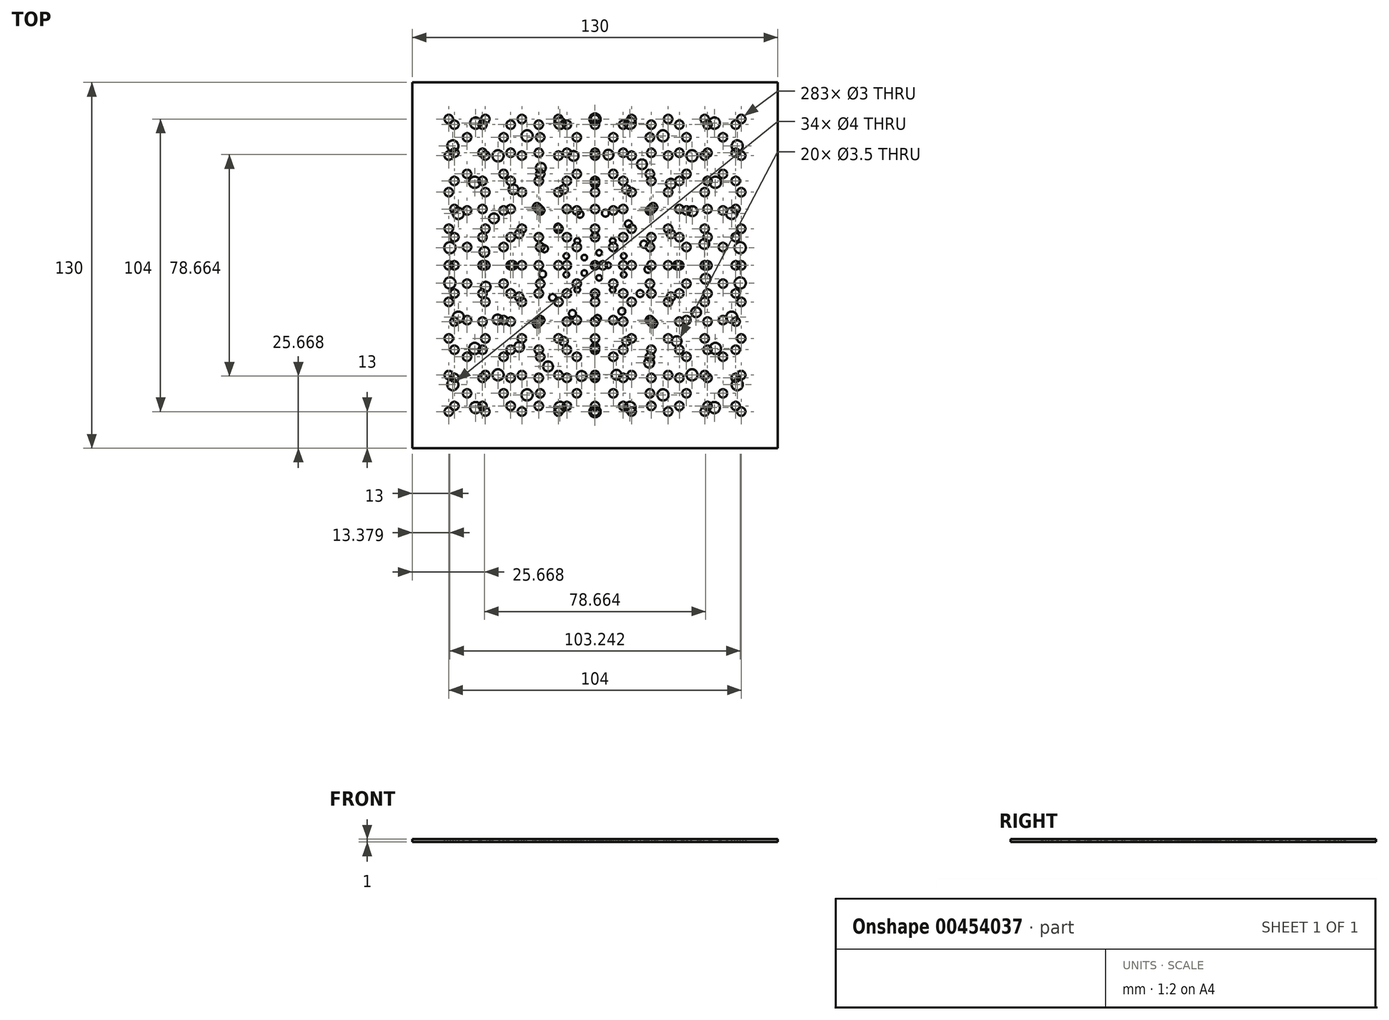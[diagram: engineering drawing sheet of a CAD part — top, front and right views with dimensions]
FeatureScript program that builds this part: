
annotation { "Feature Type Name" : "Feature", "Feature Type Description" : "" }
export const myFeature = defineFeature(function(context is Context, id is Id, definition is map)
    precondition{}
    {
        {
            var Q0;
            Q0=qCreatedBy(makeId("Top.planeOp"),FACE);
            var sketch = newSketch(context, id + "F0", { "sketchPlane" : qUnion([Q0])});
            skLineSegment(sketch, "E0.bottom", {"start": v(65, 65) * mm, "end": v(-65, 65) * mm});
            skLineSegment(sketch, "E0.top", {"start": v(65, -65) * mm, "end": v(-65, -65) * mm});
            skLineSegment(sketch, "E0.left", {"start": v(65, 65) * mm, "end": v(65, -65) * mm});
            skLineSegment(sketch, "E0.right", {"start": v(-65, 65) * mm, "end": v(-65, -65) * mm});
            skPoint(sketch, "E0.middle", {"position": v(0, 0) * mm});
            skLineSegment(sketch, "E1.bottom", {"start": v(55, 55) * mm, "end": v(-55, 55) * mm, "construction": true});
            skLineSegment(sketch, "E1.top", {"start": v(55, -55) * mm, "end": v(-55, -55) * mm, "construction": true});
            skLineSegment(sketch, "E1.left", {"start": v(55, 55) * mm, "end": v(55, -55) * mm, "construction": true});
            skLineSegment(sketch, "E1.right", {"start": v(-55, 55) * mm, "end": v(-55, -55) * mm, "construction": true});
            skCircle(sketch, "E2", {"center": v(0, 0) * mm, "radius": 1.5 * mm});
            skCircle(sketch, "E3.0.1.0", {"center": v(0, 10) * mm, "radius": 1.5 * mm});
            skCircle(sketch, "E3.0.2.0", {"center": v(0, 20) * mm, "radius": 1.5 * mm});
            skCircle(sketch, "E3.0.3.0", {"center": v(0, 30) * mm, "radius": 1.5 * mm});
            skCircle(sketch, "E3.0.4.0", {"center": v(0, 40) * mm, "radius": 1.5 * mm});
            skCircle(sketch, "E3.0.5.0", {"center": v(0, 50) * mm, "radius": 1.5 * mm});
            skCircle(sketch, "E3.1.0.0", {"center": v(10, 0) * mm, "radius": 1.5 * mm});
            skCircle(sketch, "E3.1.1.0", {"center": v(10, 10) * mm, "radius": 1.5 * mm});
            skCircle(sketch, "E3.1.2.0", {"center": v(10, 20) * mm, "radius": 1.5 * mm});
            skCircle(sketch, "E3.1.3.0", {"center": v(10, 30) * mm, "radius": 1.5 * mm});
            skCircle(sketch, "E3.1.4.0", {"center": v(10, 40) * mm, "radius": 1.5 * mm});
            skCircle(sketch, "E3.1.5.0", {"center": v(10, 50) * mm, "radius": 1.5 * mm});
            skCircle(sketch, "E3.2.0.0", {"center": v(20, 0) * mm, "radius": 1.5 * mm});
            skCircle(sketch, "E3.2.1.0", {"center": v(20, 10) * mm, "radius": 1.5 * mm});
            skCircle(sketch, "E3.2.2.0", {"center": v(20, 20) * mm, "radius": 1.5 * mm});
            skCircle(sketch, "E3.2.3.0", {"center": v(20, 30) * mm, "radius": 1.5 * mm});
            skCircle(sketch, "E3.2.4.0", {"center": v(20, 40) * mm, "radius": 1.5 * mm});
            skCircle(sketch, "E3.2.5.0", {"center": v(20, 50) * mm, "radius": 1.5 * mm});
            skCircle(sketch, "E3.3.0.0", {"center": v(30, 0) * mm, "radius": 1.5 * mm});
            skCircle(sketch, "E3.3.1.0", {"center": v(30, 10) * mm, "radius": 1.5 * mm});
            skCircle(sketch, "E3.3.2.0", {"center": v(30, 20) * mm, "radius": 1.5 * mm});
            skCircle(sketch, "E3.3.3.0", {"center": v(30, 30) * mm, "radius": 1.5 * mm});
            skCircle(sketch, "E3.3.4.0", {"center": v(30, 40) * mm, "radius": 1.5 * mm});
            skCircle(sketch, "E3.3.5.0", {"center": v(30, 50) * mm, "radius": 1.5 * mm});
            skCircle(sketch, "E3.4.0.0", {"center": v(40, 0) * mm, "radius": 1.5 * mm});
            skCircle(sketch, "E3.4.1.0", {"center": v(40, 10) * mm, "radius": 1.5 * mm});
            skCircle(sketch, "E3.4.2.0", {"center": v(40, 20) * mm, "radius": 1.5 * mm});
            skCircle(sketch, "E3.4.3.0", {"center": v(40, 30) * mm, "radius": 1.5 * mm});
            skCircle(sketch, "E3.4.4.0", {"center": v(40, 40) * mm, "radius": 1.5 * mm});
            skCircle(sketch, "E3.4.5.0", {"center": v(40, 50) * mm, "radius": 1.5 * mm});
            skCircle(sketch, "E3.5.0.0", {"center": v(50, 0) * mm, "radius": 1.5 * mm});
            skCircle(sketch, "E3.5.1.0", {"center": v(50, 10) * mm, "radius": 1.5 * mm});
            skCircle(sketch, "E3.5.2.0", {"center": v(50, 20) * mm, "radius": 1.5 * mm});
            skCircle(sketch, "E3.5.3.0", {"center": v(50, 30) * mm, "radius": 1.5 * mm});
            skCircle(sketch, "E3.5.4.0", {"center": v(50, 40) * mm, "radius": 1.5 * mm});
            skCircle(sketch, "E3.5.5.0", {"center": v(50, 50) * mm, "radius": 1.5 * mm});
            skLineSegment(sketch, "E3.direction1", {"start": v(0, 0) * mm, "end": v(10, 0) * mm, "construction": true});
            skLineSegment(sketch, "E3.direction2", {"start": v(0, 0) * mm, "end": v(0, 10) * mm, "construction": true});
            skCircle(sketch, "E4.0.1.0", {"center": v(0, -10) * mm, "radius": 1.5 * mm});
            skCircle(sketch, "E4.0.2.0", {"center": v(0, -20) * mm, "radius": 1.5 * mm});
            skCircle(sketch, "E4.0.3.0", {"center": v(0, -30) * mm, "radius": 1.5 * mm});
            skCircle(sketch, "E4.0.4.0", {"center": v(0, -40) * mm, "radius": 1.5 * mm});
            skCircle(sketch, "E4.0.5.0", {"center": v(0, -50) * mm, "radius": 1.5 * mm});
            skCircle(sketch, "E4.1.1.0", {"center": v(10, -10) * mm, "radius": 1.5 * mm});
            skCircle(sketch, "E4.1.2.0", {"center": v(10, -20) * mm, "radius": 1.5 * mm});
            skCircle(sketch, "E4.1.3.0", {"center": v(10, -30) * mm, "radius": 1.5 * mm});
            skCircle(sketch, "E4.1.4.0", {"center": v(10, -40) * mm, "radius": 1.5 * mm});
            skCircle(sketch, "E4.1.5.0", {"center": v(10, -50) * mm, "radius": 1.5 * mm});
            skCircle(sketch, "E4.2.1.0", {"center": v(20, -10) * mm, "radius": 1.5 * mm});
            skCircle(sketch, "E4.2.2.0", {"center": v(20, -20) * mm, "radius": 1.5 * mm});
            skCircle(sketch, "E4.2.3.0", {"center": v(20, -30) * mm, "radius": 1.5 * mm});
            skCircle(sketch, "E4.2.4.0", {"center": v(20, -40) * mm, "radius": 1.5 * mm});
            skCircle(sketch, "E4.2.5.0", {"center": v(20, -50) * mm, "radius": 1.5 * mm});
            skCircle(sketch, "E4.3.1.0", {"center": v(30, -10) * mm, "radius": 1.5 * mm});
            skCircle(sketch, "E4.3.2.0", {"center": v(30, -20) * mm, "radius": 1.5 * mm});
            skCircle(sketch, "E4.3.3.0", {"center": v(30, -30) * mm, "radius": 1.5 * mm});
            skCircle(sketch, "E4.3.4.0", {"center": v(30, -40) * mm, "radius": 1.5 * mm});
            skCircle(sketch, "E4.3.5.0", {"center": v(30, -50) * mm, "radius": 1.5 * mm});
            skCircle(sketch, "E4.4.1.0", {"center": v(40, -10) * mm, "radius": 1.5 * mm});
            skCircle(sketch, "E4.4.2.0", {"center": v(40, -20) * mm, "radius": 1.5 * mm});
            skCircle(sketch, "E4.4.3.0", {"center": v(40, -30) * mm, "radius": 1.5 * mm});
            skCircle(sketch, "E4.4.4.0", {"center": v(40, -40) * mm, "radius": 1.5 * mm});
            skCircle(sketch, "E4.4.5.0", {"center": v(40, -50) * mm, "radius": 1.5 * mm});
            skCircle(sketch, "E4.5.1.0", {"center": v(50, -10) * mm, "radius": 1.5 * mm});
            skCircle(sketch, "E4.5.2.0", {"center": v(50, -20) * mm, "radius": 1.5 * mm});
            skCircle(sketch, "E4.5.3.0", {"center": v(50, -30) * mm, "radius": 1.5 * mm});
            skCircle(sketch, "E4.5.4.0", {"center": v(50, -40) * mm, "radius": 1.5 * mm});
            skCircle(sketch, "E4.5.5.0", {"center": v(50, -50) * mm, "radius": 1.5 * mm});
            skLineSegment(sketch, "E4.direction2", {"start": v(0, 0) * mm, "end": v(0, -10) * mm, "construction": true});
            skCircle(sketch, "E5.1.0.0", {"center": v(-10, -50) * mm, "radius": 1.5 * mm});
            skCircle(sketch, "E5.1.1.0", {"center": v(-10, -40) * mm, "radius": 1.5 * mm});
            skCircle(sketch, "E5.1.2.0", {"center": v(-10, -30) * mm, "radius": 1.5 * mm});
            skCircle(sketch, "E5.1.3.0", {"center": v(-10, -20) * mm, "radius": 1.5 * mm});
            skCircle(sketch, "E5.1.4.0", {"center": v(-10, -10) * mm, "radius": 1.5 * mm});
            skCircle(sketch, "E5.1.5.0", {"center": v(-10, 0) * mm, "radius": 1.5 * mm});
            skCircle(sketch, "E5.1.6.0", {"center": v(-10, 10) * mm, "radius": 1.5 * mm});
            skCircle(sketch, "E5.1.7.0", {"center": v(-10, 20) * mm, "radius": 1.5 * mm});
            skCircle(sketch, "E5.1.8.0", {"center": v(-10, 30) * mm, "radius": 1.5 * mm});
            skCircle(sketch, "E5.1.9.0", {"center": v(-10, 40) * mm, "radius": 1.5 * mm});
            skCircle(sketch, "E5.1.10.0", {"center": v(-10, 50) * mm, "radius": 1.5 * mm});
            skCircle(sketch, "E5.2.0.0", {"center": v(-20, -50) * mm, "radius": 1.5 * mm});
            skCircle(sketch, "E5.2.1.0", {"center": v(-20, -40) * mm, "radius": 1.5 * mm});
            skCircle(sketch, "E5.2.2.0", {"center": v(-20, -30) * mm, "radius": 1.5 * mm});
            skCircle(sketch, "E5.2.3.0", {"center": v(-20, -20) * mm, "radius": 1.5 * mm});
            skCircle(sketch, "E5.2.4.0", {"center": v(-20, -10) * mm, "radius": 1.5 * mm});
            skCircle(sketch, "E5.2.5.0", {"center": v(-20, 0) * mm, "radius": 1.5 * mm});
            skCircle(sketch, "E5.2.6.0", {"center": v(-20, 10) * mm, "radius": 1.5 * mm});
            skCircle(sketch, "E5.2.7.0", {"center": v(-20, 20) * mm, "radius": 1.5 * mm});
            skCircle(sketch, "E5.2.8.0", {"center": v(-20, 30) * mm, "radius": 1.5 * mm});
            skCircle(sketch, "E5.2.9.0", {"center": v(-20, 40) * mm, "radius": 1.5 * mm});
            skCircle(sketch, "E5.2.10.0", {"center": v(-20, 50) * mm, "radius": 1.5 * mm});
            skCircle(sketch, "E5.3.0.0", {"center": v(-30, -50) * mm, "radius": 1.5 * mm});
            skCircle(sketch, "E5.3.1.0", {"center": v(-30, -40) * mm, "radius": 1.5 * mm});
            skCircle(sketch, "E5.3.2.0", {"center": v(-30, -30) * mm, "radius": 1.5 * mm});
            skCircle(sketch, "E5.3.3.0", {"center": v(-30, -20) * mm, "radius": 1.5 * mm});
            skCircle(sketch, "E5.3.4.0", {"center": v(-30, -10) * mm, "radius": 1.5 * mm});
            skCircle(sketch, "E5.3.5.0", {"center": v(-30, 0) * mm, "radius": 1.5 * mm});
            skCircle(sketch, "E5.3.6.0", {"center": v(-30, 10) * mm, "radius": 1.5 * mm});
            skCircle(sketch, "E5.3.7.0", {"center": v(-30, 20) * mm, "radius": 1.5 * mm});
            skCircle(sketch, "E5.3.8.0", {"center": v(-30, 30) * mm, "radius": 1.5 * mm});
            skCircle(sketch, "E5.3.9.0", {"center": v(-30, 40) * mm, "radius": 1.5 * mm});
            skCircle(sketch, "E5.3.10.0", {"center": v(-30, 50) * mm, "radius": 1.5 * mm});
            skCircle(sketch, "E5.4.0.0", {"center": v(-40, -50) * mm, "radius": 1.5 * mm});
            skCircle(sketch, "E5.4.1.0", {"center": v(-40, -40) * mm, "radius": 1.5 * mm});
            skCircle(sketch, "E5.4.2.0", {"center": v(-40, -30) * mm, "radius": 1.5 * mm});
            skCircle(sketch, "E5.4.3.0", {"center": v(-40, -20) * mm, "radius": 1.5 * mm});
            skCircle(sketch, "E5.4.4.0", {"center": v(-40, -10) * mm, "radius": 1.5 * mm});
            skCircle(sketch, "E5.4.5.0", {"center": v(-40, 0) * mm, "radius": 1.5 * mm});
            skCircle(sketch, "E5.4.6.0", {"center": v(-40, 10) * mm, "radius": 1.5 * mm});
            skCircle(sketch, "E5.4.7.0", {"center": v(-40, 20) * mm, "radius": 1.5 * mm});
            skCircle(sketch, "E5.4.8.0", {"center": v(-40, 30) * mm, "radius": 1.5 * mm});
            skCircle(sketch, "E5.4.9.0", {"center": v(-40, 40) * mm, "radius": 1.5 * mm});
            skCircle(sketch, "E5.4.10.0", {"center": v(-40, 50) * mm, "radius": 1.5 * mm});
            skCircle(sketch, "E5.5.0.0", {"center": v(-50, -50) * mm, "radius": 1.5 * mm});
            skCircle(sketch, "E5.5.1.0", {"center": v(-50, -40) * mm, "radius": 1.5 * mm});
            skCircle(sketch, "E5.5.2.0", {"center": v(-50, -30) * mm, "radius": 1.5 * mm});
            skCircle(sketch, "E5.5.3.0", {"center": v(-50, -20) * mm, "radius": 1.5 * mm});
            skCircle(sketch, "E5.5.4.0", {"center": v(-50, -10) * mm, "radius": 1.5 * mm});
            skCircle(sketch, "E5.5.5.0", {"center": v(-50, 0) * mm, "radius": 1.5 * mm});
            skCircle(sketch, "E5.5.6.0", {"center": v(-50, 10) * mm, "radius": 1.5 * mm});
            skCircle(sketch, "E5.5.7.0", {"center": v(-50, 20) * mm, "radius": 1.5 * mm});
            skCircle(sketch, "E5.5.8.0", {"center": v(-50, 30) * mm, "radius": 1.5 * mm});
            skCircle(sketch, "E5.5.9.0", {"center": v(-50, 40) * mm, "radius": 1.5 * mm});
            skCircle(sketch, "E5.5.10.0", {"center": v(-50, 50) * mm, "radius": 1.5 * mm});
            skLineSegment(sketch, "E5.direction1", {"start": v(0, -50) * mm, "end": v(-10, -50) * mm, "construction": true});
            skLineSegment(sketch, "E5.direction2", {"start": v(0, -50) * mm, "end": v(0, -40) * mm, "construction": true});
            skSolve(sketch);
        }
        {
            var Q0;
            Q0=makeQuery(id+"F0.imprint","IMPRINT",FACE,{"disambiguationData":[TD([[makeQuery(id+"F0.imprint","IMPRINT",EDGE,{"derivedFrom":sQuery(id+"F0.wireOp",EDGE,"E0.bottom")}),1.0]])]});
            extrude(context, id + "F1", {"entities" : qUnion([Q0]), "depth" : 1 * mm});
        }
        {
            var Q0;
            Q0=qCreatedBy(makeId("Top.planeOp"),FACE);
            var sketch = newSketch(context, id + "F2", { "sketchPlane" : qUnion([Q0])});
            skLineSegment(sketch, "E6.bottom", {"start": v(65, 65) * mm, "end": v(-65, 65) * mm});
            skLineSegment(sketch, "E6.top", {"start": v(65, -65) * mm, "end": v(-65, -65) * mm});
            skLineSegment(sketch, "E6.left", {"start": v(65, 65) * mm, "end": v(65, -65) * mm});
            skLineSegment(sketch, "E6.right", {"start": v(-65, 65) * mm, "end": v(-65, -65) * mm});
            skPoint(sketch, "E6.middle", {"position": v(0, 0) * mm});
            skLineSegment(sketch, "E7.bottom", {"start": v(55, 55) * mm, "end": v(-55, 55) * mm, "construction": true});
            skLineSegment(sketch, "E7.top", {"start": v(55, -55) * mm, "end": v(-55, -55) * mm, "construction": true});
            skLineSegment(sketch, "E7.left", {"start": v(55, 55) * mm, "end": v(55, -55) * mm, "construction": true});
            skLineSegment(sketch, "E7.right", {"start": v(-55, 55) * mm, "end": v(-55, -55) * mm, "construction": true});
            skCircle(sketch, "E8", {"center": v(0, 52) * mm, "radius": 2 * mm});
            skCircle(sketch, "E9.1.0", {"center": v(-12.44, 50.49) * mm, "radius": 2 * mm});
            skCircle(sketch, "E9.2.0", {"center": v(-24.17, 46.04) * mm, "radius": 2 * mm});
            skCircle(sketch, "E9.3.0", {"center": v(-34.48, 38.92) * mm, "radius": 2 * mm});
            skCircle(sketch, "E9.4.0", {"center": v(-42.8, 29.54) * mm, "radius": 2 * mm});
            skCircle(sketch, "E9.5.0", {"center": v(-48.62, 18.44) * mm, "radius": 2 * mm});
            skCircle(sketch, "E9.6.0", {"center": v(-51.62, 6.27) * mm, "radius": 2 * mm});
            skCircle(sketch, "E9.7.0", {"center": v(-51.62, -6.27) * mm, "radius": 2 * mm});
            skCircle(sketch, "E9.8.0", {"center": v(-48.62, -18.44) * mm, "radius": 2 * mm});
            skCircle(sketch, "E9.9.0", {"center": v(-42.8, -29.54) * mm, "radius": 2 * mm});
            skCircle(sketch, "E9.10.0", {"center": v(-34.48, -38.92) * mm, "radius": 2 * mm});
            skCircle(sketch, "E9.11.0", {"center": v(-24.17, -46.04) * mm, "radius": 2 * mm});
            skCircle(sketch, "E9.12.0", {"center": v(-12.44, -50.49) * mm, "radius": 2 * mm});
            skCircle(sketch, "E9.13.0", {"center": v(0, -52) * mm, "radius": 2 * mm});
            skCircle(sketch, "E9.14.0", {"center": v(12.44, -50.49) * mm, "radius": 2 * mm});
            skCircle(sketch, "E9.15.0", {"center": v(24.17, -46.04) * mm, "radius": 2 * mm});
            skCircle(sketch, "E9.16.0", {"center": v(34.48, -38.92) * mm, "radius": 2 * mm});
            skCircle(sketch, "E9.17.0", {"center": v(42.8, -29.54) * mm, "radius": 2 * mm});
            skCircle(sketch, "E9.18.0", {"center": v(48.62, -18.44) * mm, "radius": 2 * mm});
            skCircle(sketch, "E9.19.0", {"center": v(51.62, -6.27) * mm, "radius": 2 * mm});
            skLineSegment(sketch, "E10", {"start": v(0, 52) * mm, "end": v(12.44, 50.49) * mm, "construction": true});
            skLineSegment(sketch, "E11", {"start": v(0, 0) * mm, "end": v(6.22, 51.24) * mm, "construction": true});
            skCircle(sketch, "E12", {"center": v(4.78, 39.33) * mm, "radius": 1.75 * mm});
            skCircle(sketch, "E13.1.0", {"center": v(-7.61, 38.88) * mm, "radius": 1.75 * mm});
            skCircle(sketch, "E13.2.0", {"center": v(-19.26, 34.63) * mm, "radius": 1.75 * mm});
            skCircle(sketch, "E13.3.0", {"center": v(-29.01, 26.98) * mm, "radius": 1.75 * mm});
            skCircle(sketch, "E13.4.0", {"center": v(-35.93, 16.7) * mm, "radius": 1.75 * mm});
            skCircle(sketch, "E13.5.0", {"center": v(-39.33, 4.78) * mm, "radius": 1.75 * mm});
            skCircle(sketch, "E13.6.0", {"center": v(-38.88, -7.61) * mm, "radius": 1.75 * mm});
            skCircle(sketch, "E13.7.0", {"center": v(-34.63, -19.26) * mm, "radius": 1.75 * mm});
            skCircle(sketch, "E13.8.0", {"center": v(-26.98, -29.01) * mm, "radius": 1.75 * mm});
            skCircle(sketch, "E13.9.0", {"center": v(-16.7, -35.93) * mm, "radius": 1.75 * mm});
            skCircle(sketch, "E13.10.0", {"center": v(-4.78, -39.33) * mm, "radius": 1.75 * mm});
            skCircle(sketch, "E13.11.0", {"center": v(7.61, -38.88) * mm, "radius": 1.75 * mm});
            skCircle(sketch, "E13.12.0", {"center": v(19.26, -34.63) * mm, "radius": 1.75 * mm});
            skCircle(sketch, "E13.13.0", {"center": v(29.01, -26.98) * mm, "radius": 1.75 * mm});
            skCircle(sketch, "E13.14.0", {"center": v(35.93, -16.7) * mm, "radius": 1.75 * mm});
            skCircle(sketch, "E13.15.0", {"center": v(39.33, -4.78) * mm, "radius": 1.75 * mm});
            skCircle(sketch, "E13.16.0", {"center": v(38.88, 7.61) * mm, "radius": 1.75 * mm});
            skCircle(sketch, "E13.17.0", {"center": v(34.63, 19.26) * mm, "radius": 1.75 * mm});
            skCircle(sketch, "E13.18.0", {"center": v(26.98, 29.01) * mm, "radius": 1.75 * mm});
            skCircle(sketch, "E13.19.0", {"center": v(16.7, 35.93) * mm, "radius": 1.75 * mm});
            skCircle(sketch, "E14", {"center": v(0, 29.2) * mm, "radius": 1.5 * mm});
            skCircle(sketch, "E15.1.0", {"center": v(-11.17, 26.98) * mm, "radius": 1.5 * mm});
            skCircle(sketch, "E15.2.0", {"center": v(-20.65, 20.65) * mm, "radius": 1.5 * mm});
            skCircle(sketch, "E15.3.0", {"center": v(-26.98, 11.17) * mm, "radius": 1.5 * mm});
            skCircle(sketch, "E15.4.0", {"center": v(-29.2, 0) * mm, "radius": 1.5 * mm});
            skCircle(sketch, "E15.5.0", {"center": v(-26.98, -11.17) * mm, "radius": 1.5 * mm});
            skCircle(sketch, "E15.6.0", {"center": v(-20.65, -20.65) * mm, "radius": 1.5 * mm});
            skCircle(sketch, "E15.7.0", {"center": v(-11.17, -26.98) * mm, "radius": 1.5 * mm});
            skCircle(sketch, "E15.8.0", {"center": v(0, -29.2) * mm, "radius": 1.5 * mm});
            skCircle(sketch, "E15.9.0", {"center": v(11.17, -26.98) * mm, "radius": 1.5 * mm});
            skCircle(sketch, "E15.10.0", {"center": v(20.65, -20.65) * mm, "radius": 1.5 * mm});
            skCircle(sketch, "E15.11.0", {"center": v(26.98, -11.17) * mm, "radius": 1.5 * mm});
            skCircle(sketch, "E15.12.0", {"center": v(29.2, 0) * mm, "radius": 1.5 * mm});
            skCircle(sketch, "E15.13.0", {"center": v(26.98, 11.17) * mm, "radius": 1.5 * mm});
            skCircle(sketch, "E15.14.0", {"center": v(20.65, 20.65) * mm, "radius": 1.5 * mm});
            skCircle(sketch, "E16.1.20.0", {"center": v(51.62, 6.27) * mm, "radius": 2 * mm});
            skCircle(sketch, "E16.1.21.0", {"center": v(48.62, 18.44) * mm, "radius": 2 * mm});
            skCircle(sketch, "E16.1.22.0", {"center": v(42.8, 29.54) * mm, "radius": 2 * mm});
            skCircle(sketch, "E16.1.23.0", {"center": v(34.48, 38.92) * mm, "radius": 2 * mm});
            skCircle(sketch, "E16.1.24.0", {"center": v(24.17, 46.04) * mm, "radius": 2 * mm});
            skLineSegment(sketch, "E17", {"start": v(0, 29.2) * mm, "end": v(11.17, 26.98) * mm, "construction": true});
            skLineSegment(sketch, "E18", {"start": v(0, 0) * mm, "end": v(5.59, 28.09) * mm, "construction": true});
            skCircle(sketch, "E19", {"center": v(3.7, 18.56) * mm, "radius": 1.25 * mm});
            skCircle(sketch, "E20.1.0", {"center": v(-5.35, 18.15) * mm, "radius": 1.25 * mm});
            skCircle(sketch, "E20.2.0", {"center": v(-13.17, 13.58) * mm, "radius": 1.25 * mm});
            skCircle(sketch, "E20.3.0", {"center": v(-17.98, 5.9) * mm, "radius": 1.25 * mm});
            skCircle(sketch, "E20.4.0", {"center": v(-18.66, -3.13) * mm, "radius": 1.25 * mm});
            skCircle(sketch, "E20.5.0", {"center": v(-15.07, -11.44) * mm, "radius": 1.25 * mm});
            skCircle(sketch, "E20.6.0", {"center": v(-8.02, -17.13) * mm, "radius": 1.25 * mm});
            skCircle(sketch, "E20.7.0", {"center": v(0.86, -18.9) * mm, "radius": 1.25 * mm});
            skCircle(sketch, "E20.8.0", {"center": v(9.54, -16.34) * mm, "radius": 1.25 * mm});
            skCircle(sketch, "E20.9.0", {"center": v(16.04, -10.03) * mm, "radius": 1.25 * mm});
            skCircle(sketch, "E21", {"center": v(0, 10.73) * mm, "radius": 1 * mm});
            skCircle(sketch, "E22.1.0", {"center": v(-6.3, 8.68) * mm, "radius": 1 * mm});
            skCircle(sketch, "E22.2.0", {"center": v(-10.2, 3.32) * mm, "radius": 1 * mm});
            skCircle(sketch, "E22.3.0", {"center": v(-10.2, -3.32) * mm, "radius": 1 * mm});
            skCircle(sketch, "E22.4.0", {"center": v(-6.3, -8.68) * mm, "radius": 1 * mm});
            skCircle(sketch, "E23.1.15.0", {"center": v(11.17, 26.98) * mm, "radius": 1.5 * mm});
            skCircle(sketch, "E24.1.10.0", {"center": v(18.87, -1.43) * mm, "radius": 1.25 * mm});
            skCircle(sketch, "E24.1.11.0", {"center": v(17.37, 7.5) * mm, "radius": 1.25 * mm});
            skCircle(sketch, "E25.1.5.0", {"center": v(0, -10.73) * mm, "radius": 1 * mm});
            skCircle(sketch, "E25.1.6.0", {"center": v(6.3, -8.68) * mm, "radius": 1 * mm});
            skCircle(sketch, "E25.1.7.0", {"center": v(10.2, -3.32) * mm, "radius": 1 * mm});
            skCircle(sketch, "E25.1.8.0", {"center": v(10.2, 3.32) * mm, "radius": 1 * mm});
            skCircle(sketch, "E25.1.9.0", {"center": v(6.3, 8.68) * mm, "radius": 1 * mm});
            skCircle(sketch, "E26.1.12.0", {"center": v(11.9, 14.71) * mm, "radius": 1.25 * mm});
            skCircle(sketch, "E27.1.25.0", {"center": v(12.44, 50.49) * mm, "radius": 2 * mm});
            skLineSegment(sketch, "E28", {"start": v(0, 10.73) * mm, "end": v(6.3, 8.68) * mm, "construction": true});
            skLineSegment(sketch, "E29", {"start": v(0, 0) * mm, "end": v(3.15, 9.7) * mm, "construction": true});
            skCircle(sketch, "E30", {"center": v(1.45, 4.47) * mm, "radius": 1 * mm});
            skCircle(sketch, "E31.1.0", {"center": v(-3.8, 2.77) * mm, "radius": 1 * mm});
            skCircle(sketch, "E31.2.0", {"center": v(-3.8, -2.77) * mm, "radius": 1 * mm});
            skCircle(sketch, "E31.3.0", {"center": v(1.45, -4.47) * mm, "radius": 1 * mm});
            skCircle(sketch, "E31.4.0", {"center": v(4.7, 0) * mm, "radius": 1 * mm});
            skCircle(sketch, "E32", {"center": v(0, 0) * mm, "radius": 1 * mm});
            skPoint(sketch, "E33.centerSnap0", {"position": v(0, 65) * mm});
            skCircle(sketch, "E34.4.0", {"center": v(-42.42, 50.56) * mm, "radius": 2 * mm});
            skCircle(sketch, "E34.5.0", {"center": v(-50.56, 42.42) * mm, "radius": 2 * mm});
            skCircle(sketch, "E34.13.0", {"center": v(-50.56, -42.42) * mm, "radius": 2 * mm});
            skCircle(sketch, "E34.14.0", {"center": v(-42.42, -50.56) * mm, "radius": 2 * mm});
            skCircle(sketch, "E34.22.0", {"center": v(42.42, -50.56) * mm, "radius": 2 * mm});
            skCircle(sketch, "E34.23.0", {"center": v(50.56, -42.42) * mm, "radius": 2 * mm});
            skCircle(sketch, "E34.31.0", {"center": v(50.56, 42.42) * mm, "radius": 2 * mm});
            skCircle(sketch, "E35.1.32.0", {"center": v(42.42, 50.56) * mm, "radius": 2 * mm});
            skSolve(sketch);
        }
        {
            var Q0;
            Q0=makeQuery(id+"F2.imprint","IMPRINT",FACE,{"disambiguationData":[TD([[makeQuery(id+"F2.imprint","IMPRINT",EDGE,{"derivedFrom":sQuery(id+"F2.wireOp",EDGE,"E6.bottom")}),1.0]])]});
            extrude(context, id + "F3", {"entities" : qUnion([Q0]), "depth" : 1 * mm});
        }
        {
            var Q0;
            Q0=qCreatedBy(makeId("Top.planeOp"),FACE);
            var sketch = newSketch(context, id + "F4", { "sketchPlane" : qUnion([Q0])});
            skLineSegment(sketch, "E36.bottom", {"start": v(65, -65) * mm, "end": v(-65, -65) * mm});
            skLineSegment(sketch, "E36.top", {"start": v(65, 65) * mm, "end": v(-65, 65) * mm});
            skLineSegment(sketch, "E36.left", {"start": v(65, -65) * mm, "end": v(65, 65) * mm});
            skLineSegment(sketch, "E36.right", {"start": v(-65, -65) * mm, "end": v(-65, 65) * mm});
            skPoint(sketch, "E36.middle", {"position": v(0, 0) * mm});
            skLineSegment(sketch, "E37.bottom", {"start": v(55, -55) * mm, "end": v(-55, -55) * mm, "construction": true});
            skLineSegment(sketch, "E37.top", {"start": v(55, 55) * mm, "end": v(-55, 55) * mm, "construction": true});
            skLineSegment(sketch, "E37.left", {"start": v(55, -55) * mm, "end": v(55, 55) * mm, "construction": true});
            skLineSegment(sketch, "E37.right", {"start": v(-55, -55) * mm, "end": v(-55, 55) * mm, "construction": true});
            skCircle(sketch, "E38", {"center": v(0, 0) * mm, "radius": 1.5 * mm});
            skCircle(sketch, "E39", {"center": v(13, 0) * mm, "radius": 1.5 * mm});
            skLineSegment(sketch, "E40", {"start": v(0, 0) * mm, "end": v(13, 0) * mm, "construction": true});
            skLineSegment(sketch, "E41", {"start": v(6.5, 0) * mm, "end": v(6.5, 6.5) * mm, "construction": true});
            skLineSegment(sketch, "E42", {"start": v(6.5, 6.5) * mm, "end": v(0, 0) * mm, "construction": true});
            skCircle(sketch, "E43", {"center": v(6.5, 6.5) * mm, "radius": 1.5 * mm});
            skCircle(sketch, "E44.0.1.0", {"center": v(0, 13) * mm, "radius": 1.5 * mm});
            skCircle(sketch, "E44.0.1.1", {"center": v(6.5, 19.5) * mm, "radius": 1.5 * mm});
            skCircle(sketch, "E44.0.2.0", {"center": v(0, 26) * mm, "radius": 1.5 * mm});
            skCircle(sketch, "E44.0.2.1", {"center": v(6.5, 32.5) * mm, "radius": 1.5 * mm});
            skCircle(sketch, "E44.0.3.0", {"center": v(0, 39) * mm, "radius": 1.5 * mm});
            skCircle(sketch, "E44.0.3.1", {"center": v(6.5, 45.5) * mm, "radius": 1.5 * mm});
            skCircle(sketch, "E44.0.4.0", {"center": v(0, 52) * mm, "radius": 1.5 * mm});
            skCircle(sketch, "E44.1.0.1", {"center": v(19.5, 6.5) * mm, "radius": 1.5 * mm});
            skCircle(sketch, "E44.1.1.0", {"center": v(13, 13) * mm, "radius": 1.5 * mm});
            skCircle(sketch, "E44.1.1.1", {"center": v(19.5, 19.5) * mm, "radius": 1.5 * mm});
            skCircle(sketch, "E44.1.2.0", {"center": v(13, 26) * mm, "radius": 1.5 * mm});
            skCircle(sketch, "E44.1.2.1", {"center": v(19.5, 32.5) * mm, "radius": 1.5 * mm});
            skCircle(sketch, "E44.1.3.0", {"center": v(13, 39) * mm, "radius": 1.5 * mm});
            skCircle(sketch, "E44.1.3.1", {"center": v(19.5, 45.5) * mm, "radius": 1.5 * mm});
            skCircle(sketch, "E44.1.4.0", {"center": v(13, 52) * mm, "radius": 1.5 * mm});
            skCircle(sketch, "E44.2.0.0", {"center": v(26, 0) * mm, "radius": 1.5 * mm});
            skCircle(sketch, "E44.2.0.1", {"center": v(32.5, 6.5) * mm, "radius": 1.5 * mm});
            skCircle(sketch, "E44.2.1.0", {"center": v(26, 13) * mm, "radius": 1.5 * mm});
            skCircle(sketch, "E44.2.1.1", {"center": v(32.5, 19.5) * mm, "radius": 1.5 * mm});
            skCircle(sketch, "E44.2.2.0", {"center": v(26, 26) * mm, "radius": 1.5 * mm});
            skCircle(sketch, "E44.2.2.1", {"center": v(32.5, 32.5) * mm, "radius": 1.5 * mm});
            skCircle(sketch, "E44.2.3.0", {"center": v(26, 39) * mm, "radius": 1.5 * mm});
            skCircle(sketch, "E44.2.3.1", {"center": v(32.5, 45.5) * mm, "radius": 1.5 * mm});
            skCircle(sketch, "E44.2.4.0", {"center": v(26, 52) * mm, "radius": 1.5 * mm});
            skCircle(sketch, "E44.3.0.0", {"center": v(39, 0) * mm, "radius": 1.5 * mm});
            skCircle(sketch, "E44.3.0.1", {"center": v(45.5, 6.5) * mm, "radius": 1.5 * mm});
            skCircle(sketch, "E44.3.1.0", {"center": v(39, 13) * mm, "radius": 1.5 * mm});
            skCircle(sketch, "E44.3.1.1", {"center": v(45.5, 19.5) * mm, "radius": 1.5 * mm});
            skCircle(sketch, "E44.3.2.0", {"center": v(39, 26) * mm, "radius": 1.5 * mm});
            skCircle(sketch, "E44.3.2.1", {"center": v(45.5, 32.5) * mm, "radius": 1.5 * mm});
            skCircle(sketch, "E44.3.3.0", {"center": v(39, 39) * mm, "radius": 1.5 * mm});
            skCircle(sketch, "E44.3.3.1", {"center": v(45.5, 45.5) * mm, "radius": 1.5 * mm});
            skCircle(sketch, "E44.3.4.0", {"center": v(39, 52) * mm, "radius": 1.5 * mm});
            skCircle(sketch, "E44.4.0.0", {"center": v(52, 0) * mm, "radius": 1.5 * mm});
            skCircle(sketch, "E44.4.1.0", {"center": v(52, 13) * mm, "radius": 1.5 * mm});
            skCircle(sketch, "E44.4.2.0", {"center": v(52, 26) * mm, "radius": 1.5 * mm});
            skCircle(sketch, "E44.4.3.0", {"center": v(52, 39) * mm, "radius": 1.5 * mm});
            skCircle(sketch, "E44.4.4.0", {"center": v(52, 52) * mm, "radius": 1.5 * mm});
            skLineSegment(sketch, "E44.direction2", {"start": v(0, 0) * mm, "end": v(0, 13) * mm, "construction": true});
            skCircle(sketch, "E45.MirrorC", {"center": v(-13, 0) * mm, "radius": 1.5 * mm});
            skCircle(sketch, "E46.MirrorC", {"center": v(-6.5, 6.5) * mm, "radius": 1.5 * mm});
            skCircle(sketch, "E47.MirrorC", {"center": v(-45.5, 32.5) * mm, "radius": 1.5 * mm});
            skCircle(sketch, "E48.MirrorC", {"center": v(-6.5, 19.5) * mm, "radius": 1.5 * mm});
            skCircle(sketch, "E49.MirrorC", {"center": v(-52, 13) * mm, "radius": 1.5 * mm});
            skCircle(sketch, "E50.MirrorC", {"center": v(-26, 39) * mm, "radius": 1.5 * mm});
            skCircle(sketch, "E51.MirrorC", {"center": v(-19.5, 32.5) * mm, "radius": 1.5 * mm});
            skCircle(sketch, "E52.MirrorC", {"center": v(-45.5, 6.5) * mm, "radius": 1.5 * mm});
            skCircle(sketch, "E53.MirrorC", {"center": v(-39, 39) * mm, "radius": 1.5 * mm});
            skCircle(sketch, "E54.MirrorC", {"center": v(-26, 0) * mm, "radius": 1.5 * mm});
            skCircle(sketch, "E55.MirrorC", {"center": v(-19.5, 6.5) * mm, "radius": 1.5 * mm});
            skCircle(sketch, "E56.MirrorC", {"center": v(-45.5, 19.5) * mm, "radius": 1.5 * mm});
            skCircle(sketch, "E57.MirrorC", {"center": v(-52, 0) * mm, "radius": 1.5 * mm});
            skCircle(sketch, "E58.MirrorC", {"center": v(-26, 26) * mm, "radius": 1.5 * mm});
            skCircle(sketch, "E59.MirrorC", {"center": v(-19.5, 45.5) * mm, "radius": 1.5 * mm});
            skLineSegment(sketch, "E60.MirrorCS", {"start": v(-6.5, 0) * mm, "end": v(-6.5, 6.5) * mm, "construction": true});
            skCircle(sketch, "E61.MirrorC", {"center": v(-26, 52) * mm, "radius": 1.5 * mm});
            skCircle(sketch, "E62.MirrorC", {"center": v(-52, 26) * mm, "radius": 1.5 * mm});
            skCircle(sketch, "E63.MirrorC", {"center": v(-13, 13) * mm, "radius": 1.5 * mm});
            skCircle(sketch, "E64.MirrorC", {"center": v(-32.5, 45.5) * mm, "radius": 1.5 * mm});
            skCircle(sketch, "E65.MirrorC", {"center": v(-6.5, 45.5) * mm, "radius": 1.5 * mm});
            skCircle(sketch, "E66.MirrorC", {"center": v(-32.5, 19.5) * mm, "radius": 1.5 * mm});
            skCircle(sketch, "E67.MirrorC", {"center": v(-39, 0) * mm, "radius": 1.5 * mm});
            skCircle(sketch, "E68.MirrorC", {"center": v(-13, 26) * mm, "radius": 1.5 * mm});
            skCircle(sketch, "E69.MirrorC", {"center": v(-52, 39) * mm, "radius": 1.5 * mm});
            skCircle(sketch, "E70.MirrorC", {"center": v(-26, 13) * mm, "radius": 1.5 * mm});
            skCircle(sketch, "E71.MirrorC", {"center": v(-39, 52) * mm, "radius": 1.5 * mm});
            skCircle(sketch, "E72.MirrorC", {"center": v(-19.5, 19.5) * mm, "radius": 1.5 * mm});
            skCircle(sketch, "E73.MirrorC", {"center": v(-13, 52) * mm, "radius": 1.5 * mm});
            skCircle(sketch, "E74.MirrorC", {"center": v(-32.5, 32.5) * mm, "radius": 1.5 * mm});
            skCircle(sketch, "E75.MirrorC", {"center": v(-52, 52) * mm, "radius": 1.5 * mm});
            skCircle(sketch, "E76.MirrorC", {"center": v(-13, 39) * mm, "radius": 1.5 * mm});
            skCircle(sketch, "E77.MirrorC", {"center": v(-45.5, 45.5) * mm, "radius": 1.5 * mm});
            skCircle(sketch, "E78.MirrorC", {"center": v(-39, 13) * mm, "radius": 1.5 * mm});
            skCircle(sketch, "E79.MirrorC", {"center": v(-39, 26) * mm, "radius": 1.5 * mm});
            skCircle(sketch, "E80.MirrorC", {"center": v(-32.5, 6.5) * mm, "radius": 1.5 * mm});
            skCircle(sketch, "E81.MirrorC", {"center": v(-6.5, 32.5) * mm, "radius": 1.5 * mm});
            skCircle(sketch, "E82.MirrorC", {"center": v(-19.5, -6.5) * mm, "radius": 1.5 * mm});
            skCircle(sketch, "E83.MirrorC", {"center": v(-52, -13) * mm, "radius": 1.5 * mm});
            skCircle(sketch, "E84.MirrorC", {"center": v(-6.5, -45.5) * mm, "radius": 1.5 * mm});
            skCircle(sketch, "E85.MirrorC", {"center": v(-26, -26) * mm, "radius": 1.5 * mm});
            skCircle(sketch, "E86.MirrorC", {"center": v(-32.5, -32.5) * mm, "radius": 1.5 * mm});
            skCircle(sketch, "E87.MirrorC", {"center": v(-6.5, -32.5) * mm, "radius": 1.5 * mm});
            skCircle(sketch, "E88.MirrorC", {"center": v(6.5, -19.5) * mm, "radius": 1.5 * mm});
            skCircle(sketch, "E89.MirrorC", {"center": v(0, -13) * mm, "radius": 1.5 * mm});
            skCircle(sketch, "E90.MirrorC", {"center": v(6.5, -32.5) * mm, "radius": 1.5 * mm});
            skCircle(sketch, "E91.MirrorC", {"center": v(6.5, -6.5) * mm, "radius": 1.5 * mm});
            skCircle(sketch, "E92.MirrorC", {"center": v(32.5, -6.5) * mm, "radius": 1.5 * mm});
            skCircle(sketch, "E93.MirrorC", {"center": v(45.5, -45.5) * mm, "radius": 1.5 * mm});
            skCircle(sketch, "E94.MirrorC", {"center": v(52, -26) * mm, "radius": 1.5 * mm});
            skCircle(sketch, "E95.MirrorC", {"center": v(26, -52) * mm, "radius": 1.5 * mm});
            skCircle(sketch, "E96.MirrorC", {"center": v(-45.5, -6.5) * mm, "radius": 1.5 * mm});
            skCircle(sketch, "E97.MirrorC", {"center": v(-13, -26) * mm, "radius": 1.5 * mm});
            skCircle(sketch, "E98.MirrorC", {"center": v(13, -13) * mm, "radius": 1.5 * mm});
            skCircle(sketch, "E99.MirrorC", {"center": v(-26, -52) * mm, "radius": 1.5 * mm});
            skCircle(sketch, "E100.MirrorC", {"center": v(-45.5, -45.5) * mm, "radius": 1.5 * mm});
            skCircle(sketch, "E101.MirrorC", {"center": v(32.5, -45.5) * mm, "radius": 1.5 * mm});
            skCircle(sketch, "E102.MirrorC", {"center": v(-19.5, -32.5) * mm, "radius": 1.5 * mm});
            skCircle(sketch, "E103.MirrorC", {"center": v(19.5, -6.5) * mm, "radius": 1.5 * mm});
            skCircle(sketch, "E104.MirrorC", {"center": v(-13, -39) * mm, "radius": 1.5 * mm});
            skCircle(sketch, "E105.MirrorC", {"center": v(0, -26) * mm, "radius": 1.5 * mm});
            skCircle(sketch, "E106.MirrorC", {"center": v(39, -39) * mm, "radius": 1.5 * mm});
            skCircle(sketch, "E107.MirrorC", {"center": v(-26, -39) * mm, "radius": 1.5 * mm});
            skCircle(sketch, "E108.MirrorC", {"center": v(-19.5, -45.5) * mm, "radius": 1.5 * mm});
            skCircle(sketch, "E109.MirrorC", {"center": v(45.5, -6.5) * mm, "radius": 1.5 * mm});
            skCircle(sketch, "E110.MirrorC", {"center": v(32.5, -19.5) * mm, "radius": 1.5 * mm});
            skCircle(sketch, "E111.MirrorC", {"center": v(32.5, -32.5) * mm, "radius": 1.5 * mm});
            skCircle(sketch, "E112.MirrorC", {"center": v(13, -52) * mm, "radius": 1.5 * mm});
            skCircle(sketch, "E113.MirrorC", {"center": v(39, -26) * mm, "radius": 1.5 * mm});
            skCircle(sketch, "E114.MirrorC", {"center": v(-39, -52) * mm, "radius": 1.5 * mm});
            skCircle(sketch, "E115.MirrorC", {"center": v(52, -52) * mm, "radius": 1.5 * mm});
            skCircle(sketch, "E116.MirrorC", {"center": v(6.5, -45.5) * mm, "radius": 1.5 * mm});
            skCircle(sketch, "E117.MirrorC", {"center": v(19.5, -32.5) * mm, "radius": 1.5 * mm});
            skCircle(sketch, "E118.MirrorC", {"center": v(39, -13) * mm, "radius": 1.5 * mm});
            skCircle(sketch, "E119.MirrorC", {"center": v(-45.5, -19.5) * mm, "radius": 1.5 * mm});
            skCircle(sketch, "E120.MirrorC", {"center": v(-19.5, -19.5) * mm, "radius": 1.5 * mm});
            skCircle(sketch, "E121.MirrorC", {"center": v(13, -39) * mm, "radius": 1.5 * mm});
            skCircle(sketch, "E122.MirrorC", {"center": v(19.5, -19.5) * mm, "radius": 1.5 * mm});
            skCircle(sketch, "E123.MirrorC", {"center": v(-52, -39) * mm, "radius": 1.5 * mm});
            skCircle(sketch, "E124.MirrorC", {"center": v(-39, -39) * mm, "radius": 1.5 * mm});
            skCircle(sketch, "E125.MirrorC", {"center": v(39, -52) * mm, "radius": 1.5 * mm});
            skCircle(sketch, "E126.MirrorC", {"center": v(26, -13) * mm, "radius": 1.5 * mm});
            skCircle(sketch, "E127.MirrorC", {"center": v(-39, -26) * mm, "radius": 1.5 * mm});
            skCircle(sketch, "E128.MirrorC", {"center": v(-13, -13) * mm, "radius": 1.5 * mm});
            skCircle(sketch, "E129.MirrorC", {"center": v(0, -39) * mm, "radius": 1.5 * mm});
            skCircle(sketch, "E130.MirrorC", {"center": v(-39, -13) * mm, "radius": 1.5 * mm});
            skCircle(sketch, "E131.MirrorC", {"center": v(-6.5, -19.5) * mm, "radius": 1.5 * mm});
            skCircle(sketch, "E132.MirrorC", {"center": v(-52, -26) * mm, "radius": 1.5 * mm});
            skCircle(sketch, "E133.MirrorC", {"center": v(-32.5, -45.5) * mm, "radius": 1.5 * mm});
            skCircle(sketch, "E134.MirrorC", {"center": v(-45.5, -32.5) * mm, "radius": 1.5 * mm});
            skCircle(sketch, "E135.MirrorC", {"center": v(-32.5, -6.5) * mm, "radius": 1.5 * mm});
            skCircle(sketch, "E136.MirrorC", {"center": v(-13, -52) * mm, "radius": 1.5 * mm});
            skCircle(sketch, "E137.MirrorC", {"center": v(-6.5, -6.5) * mm, "radius": 1.5 * mm});
            skCircle(sketch, "E138.MirrorC", {"center": v(0, -52) * mm, "radius": 1.5 * mm});
            skCircle(sketch, "E139.MirrorC", {"center": v(19.5, -45.5) * mm, "radius": 1.5 * mm});
            skCircle(sketch, "E140.MirrorC", {"center": v(26, -26) * mm, "radius": 1.5 * mm});
            skCircle(sketch, "E141.MirrorC", {"center": v(45.5, -19.5) * mm, "radius": 1.5 * mm});
            skCircle(sketch, "E142.MirrorC", {"center": v(-52, -52) * mm, "radius": 1.5 * mm});
            skCircle(sketch, "E143.MirrorC", {"center": v(-32.5, -19.5) * mm, "radius": 1.5 * mm});
            skCircle(sketch, "E144.MirrorC", {"center": v(52, -13) * mm, "radius": 1.5 * mm});
            skCircle(sketch, "E145.MirrorC", {"center": v(26, -39) * mm, "radius": 1.5 * mm});
            skCircle(sketch, "E146.MirrorC", {"center": v(52, -39) * mm, "radius": 1.5 * mm});
            skCircle(sketch, "E147.MirrorC", {"center": v(45.5, -32.5) * mm, "radius": 1.5 * mm});
            skCircle(sketch, "E148.MirrorC", {"center": v(-26, -13) * mm, "radius": 1.5 * mm});
            skCircle(sketch, "E149.MirrorC", {"center": v(13, -26) * mm, "radius": 1.5 * mm});
            skSolve(sketch);
        }
        {
            var Q0;
            Q0=makeQuery(id+"F4.imprint","IMPRINT",FACE,{"disambiguationData":[TD([[makeQuery(id+"F4.imprint","IMPRINT",EDGE,{"derivedFrom":sQuery(id+"F4.wireOp",EDGE,"E36.bottom")}),-1.0]])]});
            extrude(context, id + "F5", {"entities" : qUnion([Q0]), "depth" : 1 * mm});
        }
        {
            var Q0;
            Q0=qCreatedBy(makeId("Top.planeOp"),FACE);
            var sketch = newSketch(context, id + "F6", { "sketchPlane" : qUnion([Q0])});
            skLineSegment(sketch, "E150.bottom", {"start": v(65, -65) * mm, "end": v(-65, -65) * mm});
            skLineSegment(sketch, "E150.top", {"start": v(65, 65) * mm, "end": v(-65, 65) * mm});
            skLineSegment(sketch, "E150.left", {"start": v(65, -65) * mm, "end": v(65, 65) * mm});
            skLineSegment(sketch, "E150.right", {"start": v(-65, -65) * mm, "end": v(-65, 65) * mm});
            skPoint(sketch, "E150.middle", {"position": v(0, 0) * mm});
            skLineSegment(sketch, "E151.bottom", {"start": v(55, -55) * mm, "end": v(-55, -55) * mm, "construction": true});
            skLineSegment(sketch, "E151.top", {"start": v(55, 55) * mm, "end": v(-55, 55) * mm, "construction": true});
            skLineSegment(sketch, "E151.left", {"start": v(55, -55) * mm, "end": v(55, 55) * mm, "construction": true});
            skLineSegment(sketch, "E151.right", {"start": v(-55, -55) * mm, "end": v(-55, 55) * mm, "construction": true});
            skCircle(sketch, "E152", {"center": v(2.78, 0) * mm, "radius": 1.5 * mm});
            skSolve(sketch);
        }
        {
            var Q0;
            Q0=makeQuery(id+"F6.imprint","IMPRINT",FACE,{"disambiguationData":[TD([[makeQuery(id+"F6.imprint","IMPRINT",EDGE,{"derivedFrom":sQuery(id+"F6.wireOp",EDGE,"E150.bottom")}),-1.0]])]});
            extrude(context, id + "F7", {"entities" : qUnion([Q0]), "depth" : 1 * mm});
        }
    });
